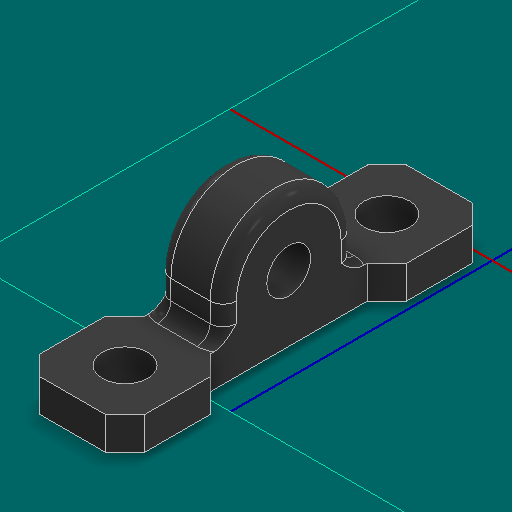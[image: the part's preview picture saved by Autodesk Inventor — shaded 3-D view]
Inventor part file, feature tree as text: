
AUTODESK INVENTOR PART (.ipt)
format: ipt  version: 2025 (Build 290162000, 162)  size: 206,336 bytes
history: native  units: in
note: dims shown in document units (in); Inventor stores cm internally (conversion verified against a paired STEP export)
features: other x3, sketch x3
ambient origin geometry x8: Origin, YZ Plane, XZ Plane, XY Plane, X Axis, Y Axis, Z Axis, Center Point
bodies: Solid1 (feature_tree)
feature tree (6):
  other  "LS Pillow Bearing Block.ipt"
  other  "Solid1::LS Pillow Bearing Block.ipt"
  other  "TaggingFeature1"
  sketch  "Sketch1"  dims[d0=0.3937in]
  sketch  "Sketch2"
  sketch  "Sketch3"
